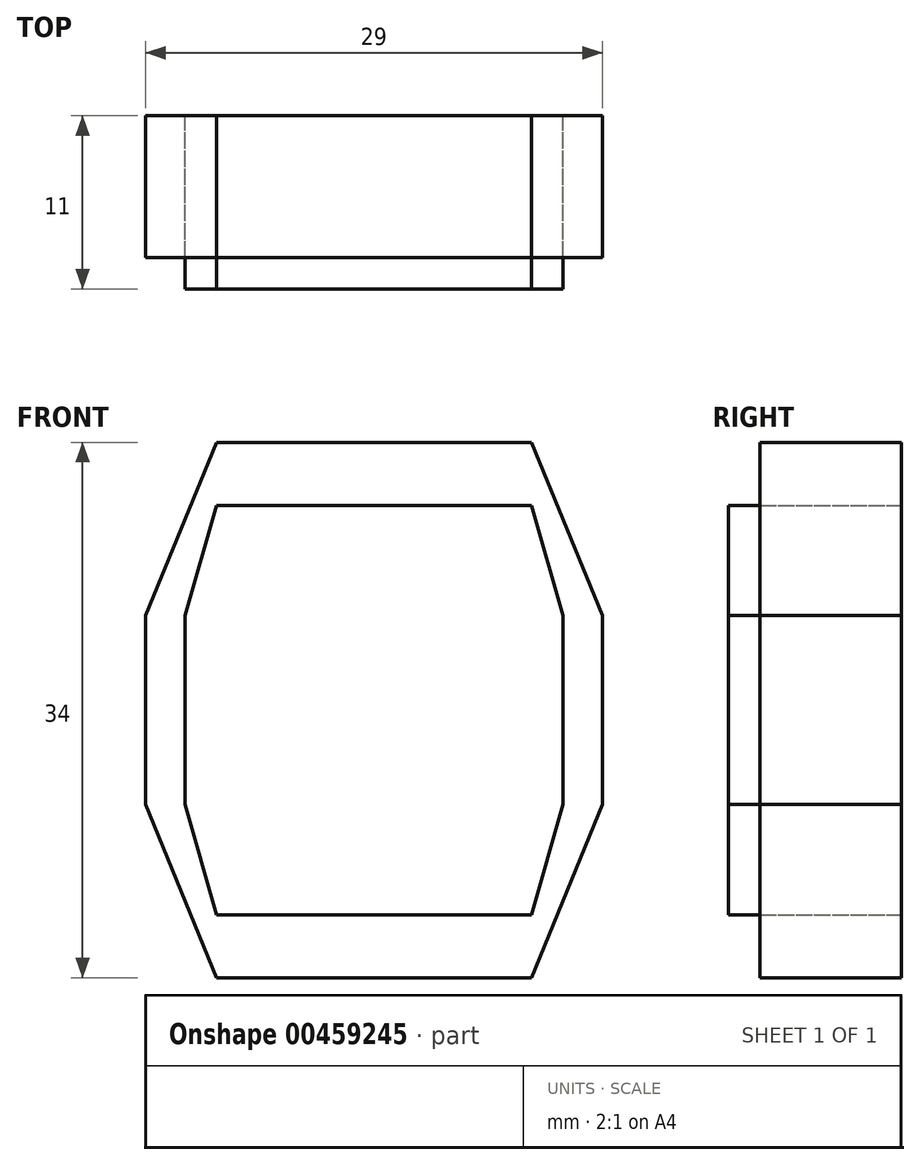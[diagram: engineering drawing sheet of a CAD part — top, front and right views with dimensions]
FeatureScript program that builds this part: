
annotation { "Feature Type Name" : "Feature", "Feature Type Description" : "" }
export const myFeature = defineFeature(function(context is Context, id is Id, definition is map)
    precondition{}
    {
        {
            var Q0;
            Q0=qCreatedBy(makeId("Front.planeOp"),FACE);
            var sketch = newSketch(context, id + "F0", { "sketchPlane" : qUnion([Q0])});
            skLineSegment(sketch, "E0", {"start": v(0, 17) * mm, "end": v(0, -17) * mm});
            skLineSegment(sketch, "E1", {"start": v(-14.5, 0) * mm, "end": v(14.5, 0) * mm});
            skLineSegment(sketch, "E2.0", {"start": v(-14.5, 6) * mm, "end": v(-14.5, -6) * mm});
            skLineSegment(sketch, "E3.0", {"start": v(14.5, 6) * mm, "end": v(14.5, -6) * mm});
            skLineSegment(sketch, "E4.0", {"start": v(-10, -17) * mm, "end": v(10, -17) * mm});
            skLineSegment(sketch, "E5.0", {"start": v(-10, 17) * mm, "end": v(10, 17) * mm});
            skPoint(sketch, "E6.orphan", {"position": v(0, 62.85) * mm});
            skPoint(sketch, "E7.orphan", {"position": v(-68.9, 0) * mm});
            skLineSegment(sketch, "E8", {"start": v(10, 17) * mm, "end": v(14.5, 6) * mm});
            skLineSegment(sketch, "E9", {"start": v(14.5, -6) * mm, "end": v(10, -17) * mm});
            skLineSegment(sketch, "E10", {"start": v(-10, -17) * mm, "end": v(-14.5, -6) * mm});
            skLineSegment(sketch, "E11", {"start": v(-14.5, 6) * mm, "end": v(-10, 17) * mm});
            skSolve(sketch);
        }
        {
            var Q0;
            Q0 = qSketchRegion(id + "F0", true);
            extrude(context, id + "F1", {"entities" : qUnion([Q0]), "depth" : 9 * mm});
        }
        {
            var Q0;
            Q0=qCreatedBy(makeId("Front.planeOp"),FACE);
            var sketch = newSketch(context, id + "F2", { "sketchPlane" : qUnion([Q0])});
            skLineSegment(sketch, "E12.0", {"start": v(-12, 6) * mm, "end": v(-12, -6) * mm});
            skLineSegment(sketch, "E13.0", {"start": v(12, 6) * mm, "end": v(12, -6) * mm});
            skLineSegment(sketch, "E14.0", {"start": v(-10, -13) * mm, "end": v(10, -13) * mm});
            skLineSegment(sketch, "E15.0", {"start": v(-10, 13) * mm, "end": v(10, 13) * mm});
            skLineSegment(sketch, "E16", {"start": v(-12, 6) * mm, "end": v(-10, 13) * mm});
            skLineSegment(sketch, "E17", {"start": v(10, 13) * mm, "end": v(12, 6) * mm});
            skLineSegment(sketch, "E18", {"start": v(12, -6) * mm, "end": v(10, -13) * mm});
            skLineSegment(sketch, "E19", {"start": v(-10, -13) * mm, "end": v(-12, -6) * mm});
            skSolve(sketch);
        }
        {
            var Q0;
            Q0 = qSketchRegion(id + "F2", true);
            extrude(context, id + "F3", {"entities" : qUnion([Q0]), "depth" : 11 * mm});
        }
    });
